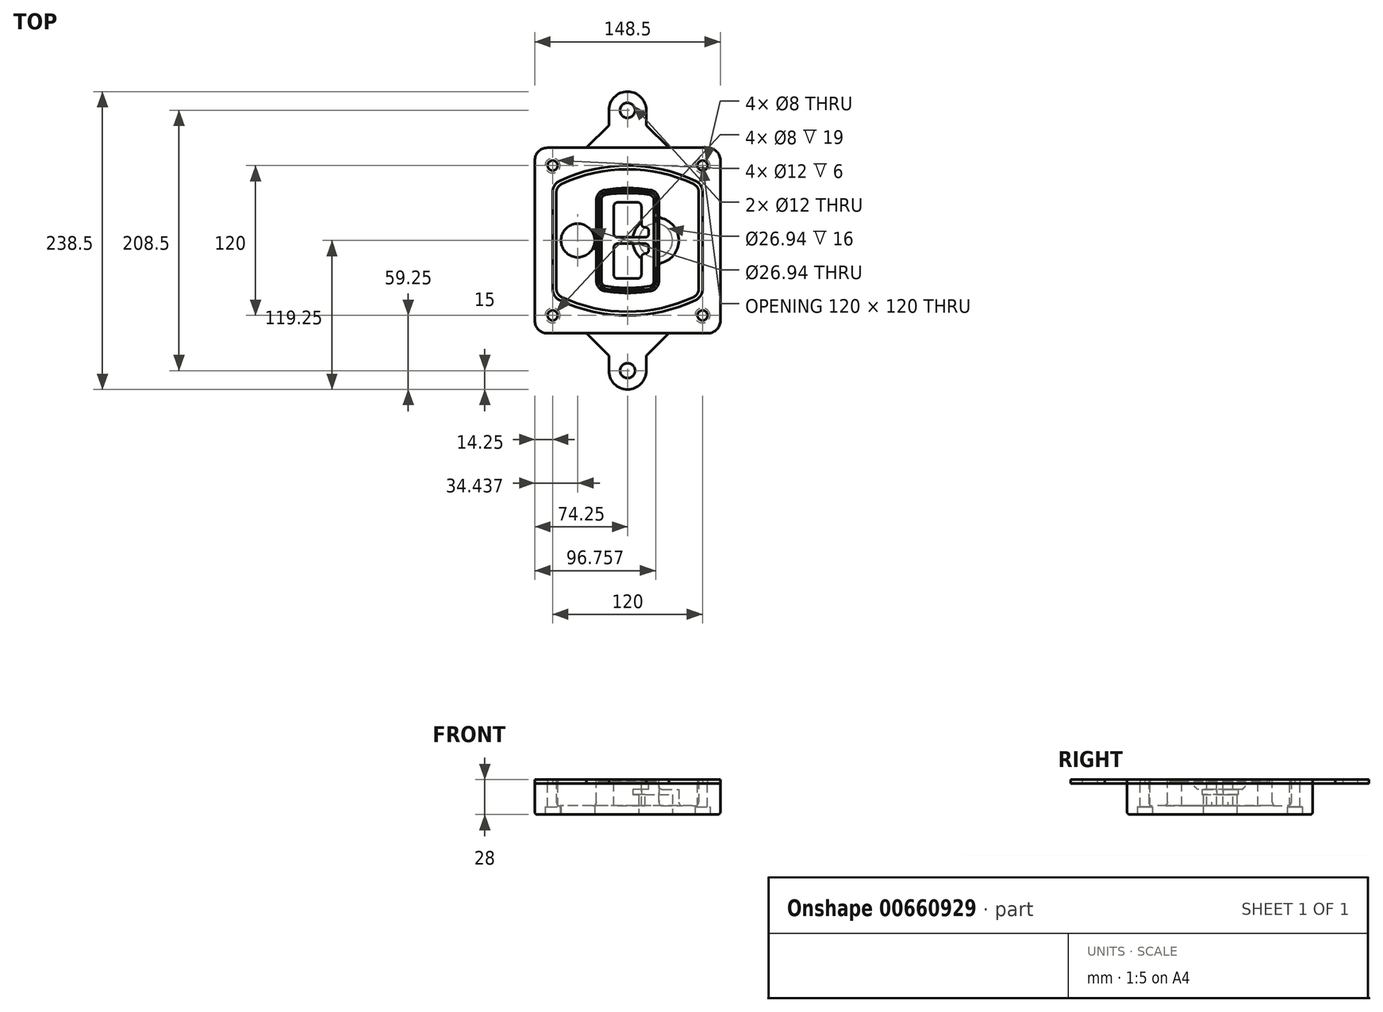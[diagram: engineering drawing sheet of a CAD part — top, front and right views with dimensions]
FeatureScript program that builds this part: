
annotation { "Feature Type Name" : "Feature", "Feature Type Description" : "" }
export const myFeature = defineFeature(function(context is Context, id is Id, definition is map)
    precondition{}
    {
        {
            var Q0;
            Q0=qCreatedBy(makeId("Top.planeOp"),FACE);
            var sketch = newSketch(context, id + "F0", { "sketchPlane" : qUnion([Q0])});
            skPoint(sketch, "E0.rect.middle", {"position": v(0, 0) * mm});
            skLineSegment(sketch, "E1.bottom", {"start": v(-64.25, -74.25) * mm, "end": v(64.25, -74.25) * mm});
            skLineSegment(sketch, "E1.top", {"start": v(-64.25, 74.25) * mm, "end": v(64.25, 74.25) * mm});
            skLineSegment(sketch, "E1.left", {"start": v(-74.25, -64.25) * mm, "end": v(-74.25, 64.25) * mm});
            skLineSegment(sketch, "E1.right", {"start": v(74.25, -64.25) * mm, "end": v(74.25, 64.25) * mm});
            skLineSegment(sketch, "E2", {"start": v(-74.25, 74.25) * mm, "end": v(74.25, -74.25) * mm, "construction": true});
            skLineSegment(sketch, "E3", {"start": v(74.25, 74.25) * mm, "end": v(-74.25, -74.25) * mm, "construction": true});
            skCircle(sketch, "E4", {"center": v(-60, 60) * mm, "radius": 4 * mm});
            skCircle(sketch, "E5", {"center": v(60, 60) * mm, "radius": 4 * mm});
            skCircle(sketch, "E6", {"center": v(60, -60) * mm, "radius": 4 * mm});
            skCircle(sketch, "E7", {"center": v(-60, -60) * mm, "radius": 4 * mm});
            skLineSegment(sketch, "E8", {"start": v(-60, 60) * mm, "end": v(60, 60) * mm, "construction": true});
            skLineSegment(sketch, "E9", {"start": v(60, 60) * mm, "end": v(60, -60) * mm, "construction": true});
            skLineSegment(sketch, "E10", {"start": v(60, -60) * mm, "end": v(-60, -60) * mm, "construction": true});
            skLineSegment(sketch, "E11", {"start": v(-60, -60) * mm, "end": v(-60, 60) * mm, "construction": true});
            skLineSegment(sketch, "E12", {"start": v(-60, 38.83) * mm, "end": v(-60, -38.83) * mm});
            skLineSegment(sketch, "E13", {"start": v(60, 38.83) * mm, "end": v(60, -38.83) * mm});
            skArc(sketch, "E14", {"start": v(54.26, 47.88) * mm, "mid": v(0, 60) * mm, "end": v(-54.26, 47.88) * mm});
            skArc(sketch, "E15", {"start": v(-54.26, -47.88) * mm, "mid": v(0, -60) * mm, "end": v(54.26, -47.88) * mm});
            skLineSegment(sketch, "E16", {"start": v(-60, 0) * mm, "end": v(60, 0) * mm, "construction": true});
            skPoint(sketch, "E17.visualSharp", {"position": v(-60, -45) * mm});
            skArc(sketch, "E17.filletArc", {"start": v(-60, -38.83) * mm, "mid": v(-58.44, -44.2) * mm, "end": v(-54.26, -47.88) * mm});
            skPoint(sketch, "E18.visualSharp", {"position": v(-60, 45) * mm});
            skArc(sketch, "E18.filletArc", {"start": v(-54.26, 47.88) * mm, "mid": v(-58.44, 44.2) * mm, "end": v(-60, 38.83) * mm});
            skPoint(sketch, "E19.visualSharp", {"position": v(60, 45) * mm});
            skArc(sketch, "E19.filletArc", {"start": v(60, 38.83) * mm, "mid": v(58.44, 44.2) * mm, "end": v(54.26, 47.88) * mm});
            skPoint(sketch, "E20.visualSharp", {"position": v(60, -45) * mm});
            skArc(sketch, "E20.filletArc", {"start": v(54.26, -47.88) * mm, "mid": v(58.44, -44.2) * mm, "end": v(60, -38.83) * mm});
            skPoint(sketch, "E21.visualSharp", {"position": v(-74.25, 74.25) * mm});
            skArc(sketch, "E21.filletArc", {"start": v(-64.25, 74.25) * mm, "mid": v(-71.32, 71.32) * mm, "end": v(-74.25, 64.25) * mm});
            skPoint(sketch, "E22.visualSharp", {"position": v(74.25, 74.25) * mm});
            skArc(sketch, "E22.filletArc", {"start": v(74.25, 64.25) * mm, "mid": v(71.32, 71.32) * mm, "end": v(64.25, 74.25) * mm});
            skPoint(sketch, "E23.visualSharp", {"position": v(74.25, -74.25) * mm});
            skArc(sketch, "E23.filletArc", {"start": v(64.25, -74.25) * mm, "mid": v(71.32, -71.32) * mm, "end": v(74.25, -64.25) * mm});
            skPoint(sketch, "E24.visualSharp", {"position": v(-74.25, -74.25) * mm});
            skArc(sketch, "E24.filletArc", {"start": v(-74.25, -64.25) * mm, "mid": v(-71.32, -71.32) * mm, "end": v(-64.25, -74.25) * mm});
            skArc(sketch, "E25.0", {"start": v(57, 38.83) * mm, "mid": v(55.9, 42.58) * mm, "end": v(52.98, 45.17) * mm});
            skLineSegment(sketch, "E25.1", {"start": v(57, 38.83) * mm, "end": v(57, -38.83) * mm});
            skArc(sketch, "E25.2", {"start": v(52.98, -45.17) * mm, "mid": v(55.9, -42.58) * mm, "end": v(57, -38.83) * mm});
            skArc(sketch, "E25.3", {"start": v(-52.98, -45.17) * mm, "mid": v(0, -57) * mm, "end": v(52.98, -45.17) * mm});
            skArc(sketch, "E25.4", {"start": v(-57, -38.83) * mm, "mid": v(-55.9, -42.58) * mm, "end": v(-52.98, -45.17) * mm});
            skArc(sketch, "E25.5", {"start": v(52.98, 45.17) * mm, "mid": v(0, 57) * mm, "end": v(-52.98, 45.17) * mm});
            skLineSegment(sketch, "E25.6", {"start": v(-57, 38.83) * mm, "end": v(-57, -38.83) * mm});
            skArc(sketch, "E25.7", {"start": v(-52.98, 45.17) * mm, "mid": v(-55.9, 42.58) * mm, "end": v(-57, 38.83) * mm});
            skArc(sketch, "E26.0", {"start": v(-55.96, 51.5) * mm, "mid": v(-61.82, 46.33) * mm, "end": v(-64, 38.83) * mm});
            skArc(sketch, "E26.1", {"start": v(55.96, 51.5) * mm, "mid": v(0, 64) * mm, "end": v(-55.96, 51.5) * mm});
            skArc(sketch, "E26.2", {"start": v(64, 38.83) * mm, "mid": v(61.82, 46.33) * mm, "end": v(55.96, 51.5) * mm});
            skLineSegment(sketch, "E26.3", {"start": v(64, 38.83) * mm, "end": v(64, -38.83) * mm});
            skArc(sketch, "E26.4", {"start": v(55.96, -51.5) * mm, "mid": v(61.82, -46.33) * mm, "end": v(64, -38.83) * mm});
            skLineSegment(sketch, "E26.5", {"start": v(-64, 38.83) * mm, "end": v(-64, -38.83) * mm});
            skArc(sketch, "E26.6", {"start": v(-55.96, -51.5) * mm, "mid": v(0, -64) * mm, "end": v(55.96, -51.5) * mm});
            skArc(sketch, "E26.7", {"start": v(-64, -38.83) * mm, "mid": v(-61.82, -46.33) * mm, "end": v(-55.96, -51.5) * mm});
            skSolve(sketch);
        }
        {
            var Q0;
            Q0=makeQuery(id+"F0.imprint","IMPRINT",FACE,{"disambiguationData":[TD([[makeQuery(id+"F0.imprint","IMPRINT",EDGE,{"derivedFrom":sQuery(id+"F0.wireOp",EDGE,"E1.bottom")}),1.0]])]});
            var Q1;
            Q1=makeQuery(id+"F0.imprint","IMPRINT",FACE,{"disambiguationData":[TD([[makeQuery(id+"F0.imprint","IMPRINT",EDGE,{"derivedFrom":sQuery(id+"F0.wireOp",EDGE,"E12")}),1.0]])]});
            var Q2;
            Q2=makeQuery(id+"F0.imprint","IMPRINT",FACE,{"disambiguationData":[TD([[makeQuery(id+"F0.imprint","IMPRINT",EDGE,{"derivedFrom":sQuery(id+"F0.wireOp",EDGE,"E25.0")}),1.0]])]});
            var Q3;
            Q3=makeQuery(id+"F0.imprint","IMPRINT",FACE,{"disambiguationData":[TD([[makeQuery(id+"F0.imprint","IMPRINT",EDGE,{"derivedFrom":sQuery(id+"F0.wireOp",EDGE,"E12")}),-1.0]])]});
            extrude(context, id + "F1", {"entities" : qUnion([Q0, Q1, Q2, Q3]), "oppositeDirection" : true, "depth" : 25 * mm, "offsetDistance" : 25 * mm});
        }
        {
            var Q0;
            Q0=makeQuery(id+"F0.imprint","IMPRINT",FACE,{"disambiguationData":[TD([[makeQuery(id+"F0.imprint","IMPRINT",EDGE,{"derivedFrom":sQuery(id+"F0.wireOp",EDGE,"E12")}),1.0]])]});
            extrude(context, id + "F2", {"entities" : qUnion([Q0]), "operationType" : NewBodyOperationType.ADD, "depth" : 3 * mm});
        }
        {
            var Q0;
            Q0=makeQuery(id+"F0.imprint","IMPRINT",FACE,{"disambiguationData":[TD([[makeQuery(id+"F0.imprint","IMPRINT",EDGE,{"derivedFrom":sQuery(id+"F0.wireOp",EDGE,"E25.0")}),1.0]])]});
            extrude(context, id + "F3", {"entities" : qUnion([Q0]), "operationType" : NewBodyOperationType.REMOVE, "oppositeDirection" : true, "depth" : 18 * mm});
        }
        {
            var Q0;
            Q0=makeQuery(id+"F2.opExtrude","CAP_FACE",FACE,{"disambiguationData":[OSD([sQuery(id+"F0.wireOp",EDGE,"E12"),sQuery(id+"F0.wireOp",EDGE,"E13"),sQuery(id+"F0.wireOp",EDGE,"E14"),sQuery(id+"F0.wireOp",EDGE,"E15"),sQuery(id+"F0.wireOp",EDGE,"E17.filletArc"),sQuery(id+"F0.wireOp",EDGE,"E18.filletArc"),sQuery(id+"F0.wireOp",EDGE,"E19.filletArc"),sQuery(id+"F0.wireOp",EDGE,"E20.filletArc"),sQuery(id+"F0.wireOp",EDGE,"E25.0"),sQuery(id+"F0.wireOp",EDGE,"E25.1"),sQuery(id+"F0.wireOp",EDGE,"E25.2"),sQuery(id+"F0.wireOp",EDGE,"E25.3"),sQuery(id+"F0.wireOp",EDGE,"E25.4"),sQuery(id+"F0.wireOp",EDGE,"E25.5"),sQuery(id+"F0.wireOp",EDGE,"E25.6"),sQuery(id+"F0.wireOp",EDGE,"E25.7")])],"isStart":false});
            var sketch = newSketch(context, id + "F4", { "sketchPlane" : qUnion([Q0])});
            skArc(sketch, "E27.0", {"start": v(-18.34, -40.45) * mm, "mid": v(0, -42) * mm, "end": v(18.34, -40.45) * mm});
            skArc(sketch, "E28.0", {"start": v(18.34, 40.45) * mm, "mid": v(0, 42) * mm, "end": v(-18.34, 40.45) * mm});
            skLineSegment(sketch, "E29", {"start": v(-25, 32.57) * mm, "end": v(-25, -32.57) * mm});
            skLineSegment(sketch, "E30", {"start": v(25, 32.57) * mm, "end": v(25, -32.57) * mm});
            skLineSegment(sketch, "E31", {"start": v(-25, 39.1) * mm, "end": v(25, 39.1) * mm, "construction": true});
            skLineSegment(sketch, "E32", {"start": v(-25, -39.1) * mm, "end": v(25, -39.1) * mm, "construction": true});
            skPoint(sketch, "E33.visualSharp", {"position": v(-25, 39.1) * mm});
            skArc(sketch, "E33.filletArc", {"start": v(-18.34, 40.45) * mm, "mid": v(-23.11, 37.73) * mm, "end": v(-25, 32.57) * mm});
            skPoint(sketch, "E34.visualSharp", {"position": v(25, 39.1) * mm});
            skArc(sketch, "E34.filletArc", {"start": v(25, 32.57) * mm, "mid": v(23.11, 37.73) * mm, "end": v(18.34, 40.45) * mm});
            skPoint(sketch, "E35.visualSharp", {"position": v(25, -39.1) * mm});
            skArc(sketch, "E35.filletArc", {"start": v(18.34, -40.45) * mm, "mid": v(23.11, -37.73) * mm, "end": v(25, -32.57) * mm});
            skPoint(sketch, "E36.visualSharp", {"position": v(-25, -39.1) * mm});
            skArc(sketch, "E36.filletArc", {"start": v(-25, -32.57) * mm, "mid": v(-23.11, -37.73) * mm, "end": v(-18.34, -40.45) * mm});
            skArc(sketch, "E37.0", {"start": v(52.98, 45.17) * mm, "mid": v(0, 57) * mm, "end": v(-52.98, 45.17) * mm});
            skArc(sketch, "E37.1", {"start": v(-52.98, 45.17) * mm, "mid": v(-55.9, 42.58) * mm, "end": v(-57, 38.83) * mm});
            skLineSegment(sketch, "E37.2", {"start": v(-57, 38.83) * mm, "end": v(-57, -38.83) * mm});
            skArc(sketch, "E37.3", {"start": v(-57, -38.83) * mm, "mid": v(-55.9, -42.58) * mm, "end": v(-52.98, -45.17) * mm});
            skArc(sketch, "E37.4", {"start": v(-52.98, -45.17) * mm, "mid": v(0, -57) * mm, "end": v(52.98, -45.17) * mm});
            skArc(sketch, "E37.5", {"start": v(52.98, -45.17) * mm, "mid": v(55.9, -42.58) * mm, "end": v(57, -38.83) * mm});
            skLineSegment(sketch, "E37.6", {"start": v(57, 38.83) * mm, "end": v(57, -38.83) * mm});
            skArc(sketch, "E37.7", {"start": v(57, 38.83) * mm, "mid": v(55.9, 42.58) * mm, "end": v(52.98, 45.17) * mm});
            skLineSegment(sketch, "E38.0", {"start": v(23, 32.57) * mm, "end": v(23, -32.57) * mm});
            skArc(sketch, "E38.1", {"start": v(18, -38.48) * mm, "mid": v(21.58, -36.44) * mm, "end": v(23, -32.57) * mm});
            skArc(sketch, "E38.2", {"start": v(-18, -38.48) * mm, "mid": v(0, -40) * mm, "end": v(18, -38.48) * mm});
            skArc(sketch, "E38.3", {"start": v(-23, -32.57) * mm, "mid": v(-21.58, -36.44) * mm, "end": v(-18, -38.48) * mm});
            skLineSegment(sketch, "E38.4", {"start": v(-23, 32.57) * mm, "end": v(-23, -32.57) * mm});
            skArc(sketch, "E38.5", {"start": v(23, 32.57) * mm, "mid": v(21.58, 36.44) * mm, "end": v(18, 38.48) * mm});
            skArc(sketch, "E38.6", {"start": v(-18, 38.48) * mm, "mid": v(-21.58, 36.44) * mm, "end": v(-23, 32.57) * mm});
            skArc(sketch, "E38.7", {"start": v(18, 38.48) * mm, "mid": v(0, 40) * mm, "end": v(-18, 38.48) * mm});
            skArc(sketch, "E39.0", {"start": v(21, 32.57) * mm, "mid": v(20.06, 35.15) * mm, "end": v(17.67, 36.5) * mm});
            skLineSegment(sketch, "E39.1", {"start": v(21, 32.57) * mm, "end": v(21, -32.57) * mm});
            skArc(sketch, "E39.2", {"start": v(17.67, -36.5) * mm, "mid": v(20.06, -35.15) * mm, "end": v(21, -32.57) * mm});
            skArc(sketch, "E39.3", {"start": v(-17.67, -36.5) * mm, "mid": v(0, -38) * mm, "end": v(17.67, -36.5) * mm});
            skArc(sketch, "E39.4", {"start": v(-21, -32.57) * mm, "mid": v(-20.06, -35.15) * mm, "end": v(-17.67, -36.5) * mm});
            skArc(sketch, "E39.5", {"start": v(17.67, 36.5) * mm, "mid": v(0, 38) * mm, "end": v(-17.67, 36.5) * mm});
            skLineSegment(sketch, "E39.6", {"start": v(-21, 32.57) * mm, "end": v(-21, -32.57) * mm});
            skArc(sketch, "E39.7", {"start": v(-17.67, 36.5) * mm, "mid": v(-20.06, 35.15) * mm, "end": v(-21, 32.57) * mm});
            skLineSegment(sketch, "E40", {"start": v(-25, 0) * mm, "end": v(25, 0) * mm, "construction": true});
            skLineSegment(sketch, "E41", {"start": v(-11, 5.5) * mm, "end": v(-11, 27.5) * mm});
            skLineSegment(sketch, "E42", {"start": v(-8, 30.5) * mm, "end": v(8, 30.5) * mm});
            skLineSegment(sketch, "E43", {"start": v(11, 27.5) * mm, "end": v(11, 13.5) * mm});
            skLineSegment(sketch, "E44", {"start": v(14, 10.5) * mm, "end": v(14, 10.5) * mm});
            skLineSegment(sketch, "E45", {"start": v(17, 7.5) * mm, "end": v(17, 5.5) * mm});
            skLineSegment(sketch, "E46", {"start": v(14, 2.5) * mm, "end": v(-8, 2.5) * mm});
            skPoint(sketch, "E47.visualSharp", {"position": v(-11, 30.5) * mm});
            skArc(sketch, "E47.filletArc", {"start": v(-8, 30.5) * mm, "mid": v(-10.12, 29.62) * mm, "end": v(-11, 27.5) * mm});
            skPoint(sketch, "E48.visualSharp", {"position": v(11, 30.5) * mm});
            skArc(sketch, "E48.filletArc", {"start": v(11, 27.5) * mm, "mid": v(10.12, 29.62) * mm, "end": v(8, 30.5) * mm});
            skPoint(sketch, "E49.visualSharp", {"position": v(11, 10.5) * mm});
            skArc(sketch, "E49.filletArc", {"start": v(11, 13.5) * mm, "mid": v(11.88, 11.38) * mm, "end": v(14, 10.5) * mm});
            skPoint(sketch, "E50.visualSharp", {"position": v(17, 10.5) * mm});
            skArc(sketch, "E50.filletArc", {"start": v(17, 7.5) * mm, "mid": v(16.12, 9.62) * mm, "end": v(14, 10.5) * mm});
            skPoint(sketch, "E51.visualSharp", {"position": v(17, 2.5) * mm});
            skArc(sketch, "E51.filletArc", {"start": v(14, 2.5) * mm, "mid": v(16.12, 3.38) * mm, "end": v(17, 5.5) * mm});
            skPoint(sketch, "E52.visualSharp", {"position": v(-11, 2.5) * mm});
            skArc(sketch, "E52.filletArc", {"start": v(-11, 5.5) * mm, "mid": v(-10.12, 3.38) * mm, "end": v(-8, 2.5) * mm});
            skLineSegment(sketch, "E53.0.MirrorCS", {"start": v(14, -2.5) * mm, "end": v(-8, -2.5) * mm});
            skArc(sketch, "E54.0.MirrorCS", {"start": v(-11, -5.5) * mm, "mid": v(-10.12, -3.38) * mm, "end": v(-8, -2.5) * mm});
            skLineSegment(sketch, "E55.0.MirrorCS", {"start": v(-11, -5.5) * mm, "end": v(-11, -27.5) * mm});
            skArc(sketch, "E56.0.MirrorCS", {"start": v(-8, -30.5) * mm, "mid": v(-10.12, -29.62) * mm, "end": v(-11, -27.5) * mm});
            skLineSegment(sketch, "E57.0.MirrorCS", {"start": v(-8, -30.5) * mm, "end": v(8, -30.5) * mm});
            skArc(sketch, "E58.0.MirrorCS", {"start": v(11, -27.5) * mm, "mid": v(10.12, -29.62) * mm, "end": v(8, -30.5) * mm});
            skLineSegment(sketch, "E59.0.MirrorCS", {"start": v(11, -27.5) * mm, "end": v(11, -13.5) * mm});
            skArc(sketch, "E60.0.MirrorCS", {"start": v(11, -13.5) * mm, "mid": v(11.88, -11.38) * mm, "end": v(14, -10.5) * mm});
            skArc(sketch, "E61.0.MirrorCS", {"start": v(17, -7.5) * mm, "mid": v(16.12, -9.62) * mm, "end": v(14, -10.5) * mm});
            skLineSegment(sketch, "E62.0.MirrorCS", {"start": v(17, -7.5) * mm, "end": v(17, -5.5) * mm});
            skArc(sketch, "E63.0.MirrorCS", {"start": v(14, -2.5) * mm, "mid": v(16.12, -3.38) * mm, "end": v(17, -5.5) * mm});
            skSolve(sketch);
        }
        {
            var Q0;
            Q0=makeQuery(id+"F4.imprint","IMPRINT",FACE,{"disambiguationData":[TD([[makeQuery(id+"F4.imprint","IMPRINT",EDGE,{"derivedFrom":sQuery(id+"F4.wireOp",EDGE,"E27.0")}),1.0]])]});
            var Q1;
            Q1=makeQuery(id+"F4.imprint","IMPRINT",FACE,{"disambiguationData":[TD([[makeQuery(id+"F4.imprint","IMPRINT",EDGE,{"derivedFrom":sQuery(id+"F4.wireOp",EDGE,"E38.0")}),-1.0]])]});
            var Q2;
            Q2=makeQuery(id+"F4.imprint","IMPRINT",FACE,{"disambiguationData":[TD([[makeQuery(id+"F4.imprint","IMPRINT",EDGE,{"derivedFrom":sQuery(id+"F4.wireOp",EDGE,"E39.0")}),1.0]])]});
            extrude(context, id + "F5", {"entities" : qUnion([Q0, Q1, Q2]), "operationType" : NewBodyOperationType.ADD, "endBound" : BoundingType.UP_TO_NEXT, "oppositeDirection" : true, "depth" : 25 * mm});
        }
        {
            var Q0;
            Q0=makeQuery(id+"F4.imprint","IMPRINT",FACE,{"disambiguationData":[TD([[makeQuery(id+"F4.imprint","IMPRINT",EDGE,{"derivedFrom":sQuery(id+"F4.wireOp",EDGE,"E38.0")}),-1.0]])]});
            extrude(context, id + "F6", {"entities" : qUnion([Q0]), "operationType" : NewBodyOperationType.REMOVE, "oppositeDirection" : true, "depth" : 2 * mm});
        }
        {
            var Q0;
            Q0=makeQuery(id+"F1.opExtrude","CAP_FACE",FACE,{"disambiguationData":[OSD([sQuery(id+"F0.wireOp",EDGE,"E1.bottom"),sQuery(id+"F0.wireOp",EDGE,"E1.top"),sQuery(id+"F0.wireOp",EDGE,"E1.left"),sQuery(id+"F0.wireOp",EDGE,"E1.right"),sQuery(id+"F0.wireOp",EDGE,"E4"),sQuery(id+"F0.wireOp",EDGE,"E5"),sQuery(id+"F0.wireOp",EDGE,"E6"),sQuery(id+"F0.wireOp",EDGE,"E7"),sQuery(id+"F0.wireOp",EDGE,"E21.filletArc"),sQuery(id+"F0.wireOp",EDGE,"E22.filletArc"),sQuery(id+"F0.wireOp",EDGE,"E23.filletArc"),sQuery(id+"F0.wireOp",EDGE,"E24.filletArc")])],"isStart":false});
            var sketch = newSketch(context, id + "F7", { "sketchPlane" : qUnion([Q0])});
            skCircle(sketch, "E64", {"center": v(22.5, 0) * mm, "radius": 13.47 * mm});
            skCircle(sketch, "E65", {"center": v(-39.81, 0) * mm, "radius": 13.47 * mm});
            skLineSegment(sketch, "E66", {"start": v(74.25, 0) * mm, "end": v(-74.25, 0) * mm});
            skCircle(sketch, "E67", {"center": v(22.5, 0) * mm, "radius": 18.47 * mm});
            skCircle(sketch, "E68", {"center": v(60, -60) * mm, "radius": 6 * mm});
            skCircle(sketch, "E69", {"center": v(-60, -60) * mm, "radius": 6 * mm});
            skCircle(sketch, "E70", {"center": v(-60, 60) * mm, "radius": 6 * mm});
            skCircle(sketch, "E71", {"center": v(60, 60) * mm, "radius": 6 * mm});
            skSolve(sketch);
        }
        {
            var Q0;
            {var subQ1=sQuery(id+"F7.wireOp",EDGE,"E66");var subQ4=sQuery(id+"F7.wireOp",EDGE,"E64");var subQ6=makeQuery(id+"F7.imprint","INTERSECT",VERTEX,{"disambiguationData":[OD(0.0)],"derivedFrom":[subQ4,subQ1]});Q0=makeQuery(id+"F7.imprint","IMPRINT",FACE,{"disambiguationData":[TD([[makeQuery(id+"F7.imprint","IMPRINT",EDGE,{"disambiguationData":[TD([[subQ6,-1.0]])],"derivedFrom":subQ4}),-1.0]])]});}
            var Q1;
            {var subQ0=sQuery(id+"F7.wireOp",EDGE,"E66");var subQ1=sQuery(id+"F7.wireOp",EDGE,"E64");var subQ3=makeQuery(id+"F7.imprint","INTERSECT",VERTEX,{"disambiguationData":[OD(0.0)],"derivedFrom":[subQ1,subQ0]});Q1=makeQuery(id+"F7.imprint","IMPRINT",FACE,{"disambiguationData":[TD([[makeQuery(id+"F7.imprint","IMPRINT",EDGE,{"disambiguationData":[TD([[subQ3,-1.0]])],"derivedFrom":subQ1}),1.0]])]});}
            var Q2;
            {var subQ0=sQuery(id+"F7.wireOp",EDGE,"E66");var subQ1=sQuery(id+"F7.wireOp",EDGE,"E64");var subQ3=makeQuery(id+"F7.imprint","INTERSECT",VERTEX,{"disambiguationData":[OD(0.0)],"derivedFrom":[subQ1,subQ0]});Q2=makeQuery(id+"F7.imprint","IMPRINT",FACE,{"disambiguationData":[TD([[makeQuery(id+"F7.imprint","IMPRINT",EDGE,{"disambiguationData":[TD([[subQ3,1.0]])],"derivedFrom":subQ1}),1.0]])]});}
            var Q3;
            {var subQ1=sQuery(id+"F7.wireOp",EDGE,"E66");var subQ4=sQuery(id+"F7.wireOp",EDGE,"E64");var subQ6=makeQuery(id+"F7.imprint","INTERSECT",VERTEX,{"disambiguationData":[OD(0.0)],"derivedFrom":[subQ4,subQ1]});Q3=makeQuery(id+"F7.imprint","IMPRINT",FACE,{"disambiguationData":[TD([[makeQuery(id+"F7.imprint","IMPRINT",EDGE,{"disambiguationData":[TD([[subQ6,1.0]])],"derivedFrom":subQ4}),-1.0]])]});}
            extrude(context, id + "F8", {"entities" : qUnion([Q0, Q1, Q2, Q3]), "operationType" : NewBodyOperationType.ADD, "oppositeDirection" : true, "depth" : 20 * mm});
        }
        {
            var Q0;
            {var subQ0=sQuery(id+"F7.wireOp",EDGE,"E66");var subQ1=sQuery(id+"F7.wireOp",EDGE,"E64");var subQ3=makeQuery(id+"F7.imprint","INTERSECT",VERTEX,{"disambiguationData":[OD(0.0)],"derivedFrom":[subQ1,subQ0]});Q0=makeQuery(id+"F7.imprint","IMPRINT",FACE,{"disambiguationData":[TD([[makeQuery(id+"F7.imprint","IMPRINT",EDGE,{"disambiguationData":[TD([[subQ3,-1.0]])],"derivedFrom":subQ1}),1.0]])]});}
            var Q1;
            {var subQ0=sQuery(id+"F7.wireOp",EDGE,"E66");var subQ1=sQuery(id+"F7.wireOp",EDGE,"E64");var subQ3=makeQuery(id+"F7.imprint","INTERSECT",VERTEX,{"disambiguationData":[OD(0.0)],"derivedFrom":[subQ1,subQ0]});Q1=makeQuery(id+"F7.imprint","IMPRINT",FACE,{"disambiguationData":[TD([[makeQuery(id+"F7.imprint","IMPRINT",EDGE,{"disambiguationData":[TD([[subQ3,1.0]])],"derivedFrom":subQ1}),1.0]])]});}
            extrude(context, id + "F9", {"entities" : qUnion([Q0, Q1]), "operationType" : NewBodyOperationType.REMOVE, "oppositeDirection" : true, "depth" : 16 * mm});
        }
        {
            var Q0;
            {var subQ0=sQuery(id+"F7.wireOp",EDGE,"E66");var subQ1=sQuery(id+"F7.wireOp",EDGE,"E65");var subQ3=makeQuery(id+"F7.imprint","INTERSECT",VERTEX,{"disambiguationData":[OD(0.0)],"derivedFrom":[subQ1,subQ0]});Q0=makeQuery(id+"F7.imprint","IMPRINT",FACE,{"disambiguationData":[TD([[makeQuery(id+"F7.imprint","IMPRINT",EDGE,{"disambiguationData":[TD([[subQ3,-1.0]])],"derivedFrom":subQ1}),1.0]])]});}
            var Q1;
            {var subQ0=sQuery(id+"F7.wireOp",EDGE,"E66");var subQ1=sQuery(id+"F7.wireOp",EDGE,"E65");var subQ3=makeQuery(id+"F7.imprint","INTERSECT",VERTEX,{"disambiguationData":[OD(0.0)],"derivedFrom":[subQ1,subQ0]});Q1=makeQuery(id+"F7.imprint","IMPRINT",FACE,{"disambiguationData":[TD([[makeQuery(id+"F7.imprint","IMPRINT",EDGE,{"disambiguationData":[TD([[subQ3,1.0]])],"derivedFrom":subQ1}),1.0]])]});}
            extrude(context, id + "F10", {"entities" : qUnion([Q0, Q1]), "operationType" : NewBodyOperationType.REMOVE, "oppositeDirection" : true, "depth" : 25 * mm});
        }
        {
            var Q0;
            Q0=makeQuery(id+"F7.imprint","IMPRINT",FACE,{"disambiguationData":[TD([[makeQuery(id+"F7.imprint","IMPRINT",EDGE,{"derivedFrom":sQuery(id+"F7.wireOp",EDGE,"E68")}),1.0]])]});
            var Q1;
            Q1=makeQuery(id+"F7.imprint","IMPRINT",FACE,{"disambiguationData":[TD([[makeQuery(id+"F7.imprint","IMPRINT",EDGE,{"derivedFrom":makeQuery(id+"F1.opExtrude","CAP_EDGE",EDGE,{"disambiguationData":[OSD([sQuery(id+"F0.wireOp",EDGE,"E5")])],"isStart":false})}),-1.0]])]});
            var Q2;
            Q2=makeQuery(id+"F7.imprint","IMPRINT",FACE,{"disambiguationData":[TD([[makeQuery(id+"F7.imprint","IMPRINT",EDGE,{"derivedFrom":sQuery(id+"F7.wireOp",EDGE,"E69")}),1.0]])]});
            var Q3;
            Q3=makeQuery(id+"F7.imprint","IMPRINT",FACE,{"disambiguationData":[TD([[makeQuery(id+"F7.imprint","IMPRINT",EDGE,{"derivedFrom":makeQuery(id+"F1.opExtrude","CAP_EDGE",EDGE,{"disambiguationData":[OSD([sQuery(id+"F0.wireOp",EDGE,"E4")])],"isStart":false})}),-1.0]])]});
            var Q4;
            Q4=makeQuery(id+"F7.imprint","IMPRINT",FACE,{"disambiguationData":[TD([[makeQuery(id+"F7.imprint","IMPRINT",EDGE,{"derivedFrom":sQuery(id+"F7.wireOp",EDGE,"E70")}),1.0]])]});
            var Q5;
            Q5=makeQuery(id+"F7.imprint","IMPRINT",FACE,{"disambiguationData":[TD([[makeQuery(id+"F7.imprint","IMPRINT",EDGE,{"derivedFrom":makeQuery(id+"F1.opExtrude","CAP_EDGE",EDGE,{"disambiguationData":[OSD([sQuery(id+"F0.wireOp",EDGE,"E7")])],"isStart":false})}),-1.0]])]});
            var Q6;
            Q6=makeQuery(id+"F7.imprint","IMPRINT",FACE,{"disambiguationData":[TD([[makeQuery(id+"F7.imprint","IMPRINT",EDGE,{"derivedFrom":sQuery(id+"F7.wireOp",EDGE,"E71")}),1.0]])]});
            var Q7;
            Q7=makeQuery(id+"F7.imprint","IMPRINT",FACE,{"disambiguationData":[TD([[makeQuery(id+"F7.imprint","IMPRINT",EDGE,{"derivedFrom":makeQuery(id+"F1.opExtrude","CAP_EDGE",EDGE,{"disambiguationData":[OSD([sQuery(id+"F0.wireOp",EDGE,"E6")])],"isStart":false})}),-1.0]])]});
            extrude(context, id + "F11", {"entities" : qUnion([Q0, Q1, Q2, Q3, Q4, Q5, Q6, Q7]), "operationType" : NewBodyOperationType.REMOVE, "oppositeDirection" : true, "depth" : 6 * mm});
        }
        {
            var Q0;
            Q0=makeQuery(id+"F9.boolean.opBoolean","COPY",FACE,{"derivedFrom":makeQuery(id+"F9.opExtrude","CAP_FACE",FACE,{"disambiguationData":[OSD([sQuery(id+"F7.wireOp",EDGE,"E64")])],"isStart":false})});
            var sketch = newSketch(context, id + "F12", { "sketchPlane" : qUnion([Q0])});
            skArc(sketch, "E72.0", {"start": v(11, 14.45) * mm, "mid": v(6.45, 9.13) * mm, "end": v(4.2, 2.5) * mm});
            skArc(sketch, "E72.1", {"start": v(4.2, -2.5) * mm, "mid": v(6.45, -9.13) * mm, "end": v(11, -14.45) * mm});
            skLineSegment(sketch, "E73", {"start": v(4.2, -2.5) * mm, "end": v(14, -2.5) * mm});
            skLineSegment(sketch, "E74.0", {"start": v(14, 2.5) * mm, "end": v(4.2, 2.5) * mm});
            skArc(sketch, "E74.1", {"start": v(14, 2.5) * mm, "mid": v(16.12, 3.38) * mm, "end": v(17, 5.5) * mm});
            skLineSegment(sketch, "E74.2", {"start": v(17, 7.5) * mm, "end": v(17, 5.5) * mm});
            skArc(sketch, "E74.3", {"start": v(17, 7.5) * mm, "mid": v(16.12, 9.62) * mm, "end": v(14, 10.5) * mm});
            skArc(sketch, "E74.4", {"start": v(11, 13.5) * mm, "mid": v(11.88, 11.38) * mm, "end": v(14, 10.5) * mm});
            skLineSegment(sketch, "E74.5", {"start": v(11, 14.45) * mm, "end": v(11, 13.5) * mm});
            skLineSegment(sketch, "E74.7", {"start": v(14, -2.5) * mm, "end": v(4.2, -2.5) * mm});
            skArc(sketch, "E74.8", {"start": v(14, -2.5) * mm, "mid": v(16.12, -3.38) * mm, "end": v(17, -5.5) * mm});
            skLineSegment(sketch, "E74.9", {"start": v(17, -7.5) * mm, "end": v(17, -5.5) * mm});
            skArc(sketch, "E74.10", {"start": v(17, -7.5) * mm, "mid": v(16.12, -9.62) * mm, "end": v(14, -10.5) * mm});
            skArc(sketch, "E74.11", {"start": v(11, -13.5) * mm, "mid": v(11.88, -11.38) * mm, "end": v(14, -10.5) * mm});
            skLineSegment(sketch, "E74.12", {"start": v(11, -14.45) * mm, "end": v(11, -13.5) * mm});
            skPoint(sketch, "E75.orphan", {"position": v(11, -27.5) * mm});
            skPoint(sketch, "E76.orphan", {"position": v(-8, -2.5) * mm});
            skPoint(sketch, "E77.orphan", {"position": v(-8, 2.5) * mm});
            skPoint(sketch, "E78.orphan", {"position": v(11, 27.5) * mm});
            skSolve(sketch);
        }
        {
            var Q0;
            {var subQ7=sQuery(id+"F12.wireOp",EDGE,"E72.0");var subQ14=sQuery(id+"F12.wireOp",EDGE,"E72.1");var subQ16=sQuery(id+"F12.wireOp",EDGE,"E74.1");var subQ18=sQuery(id+"F12.wireOp",EDGE,"E74.8");Q0=qUnion([makeQuery(id+"F12.imprint","IMPRINT",FACE,{"disambiguationData":[TD([[makeQuery(id+"F12.imprint","IMPRINT",EDGE,{"derivedFrom":subQ7}),1.0]])]}),makeQuery(id+"F12.imprint","IMPRINT",FACE,{"disambiguationData":[TD([[makeQuery(id+"F12.imprint","IMPRINT",EDGE,{"derivedFrom":subQ14}),1.0]])]}),makeQuery(id+"F12.imprint","IMPRINT",FACE,{"disambiguationData":[TD([[makeQuery(id+"F12.imprint","IMPRINT",EDGE,{"derivedFrom":subQ16}),1.0]])]}),makeQuery(id+"F12.imprint","IMPRINT",FACE,{"disambiguationData":[TD([[makeQuery(id+"F12.imprint","IMPRINT",EDGE,{"derivedFrom":subQ18}),-1.0]])]})]);}
            var Q1;
            Q1=makeQuery(id+"F5.boolean.opBoolean","SPLIT",FACE,{"disambiguationData":[TD([makeQuery(id+"F5.opExtrude","SWEPT_FACE",FACE,{"disambiguationData":[OSD([sQuery(id+"F4.wireOp",EDGE,"E41")])]})])],"derivedFrom":makeQuery(id+"F3.boolean.opBoolean","COPY",FACE,{"derivedFrom":makeQuery(id+"F3.opExtrude","CAP_FACE",FACE,{"disambiguationData":[OSD([sQuery(id+"F0.wireOp",EDGE,"E25.0"),sQuery(id+"F0.wireOp",EDGE,"E25.1"),sQuery(id+"F0.wireOp",EDGE,"E25.2"),sQuery(id+"F0.wireOp",EDGE,"E25.3"),sQuery(id+"F0.wireOp",EDGE,"E25.4"),sQuery(id+"F0.wireOp",EDGE,"E25.5"),sQuery(id+"F0.wireOp",EDGE,"E25.6"),sQuery(id+"F0.wireOp",EDGE,"E25.7")])],"isStart":false})})});
            extrude(context, id + "F13", {"entities" : qUnion([Q0]), "operationType" : NewBodyOperationType.REMOVE, "endBound" : BoundingType.UP_TO_SURFACE, "endBoundEntityFace" : qUnion([Q1]), "depth" : 25 * mm});
        }
        {
            var Q0;
            Q0=makeQuery(id+"F3.boolean.opBoolean","COPY",EDGE,{"derivedFrom":makeQuery(id+"F3.opExtrude","CAP_EDGE",EDGE,{"disambiguationData":[OSD([sQuery(id+"F0.wireOp",EDGE,"E25.6")])],"isStart":false})});
            var Q1;
            Q1=makeQuery(id+"F8.boolean.opBoolean","INTERSECT",EDGE,{"derivedFrom":[makeQuery(id+"F5.opExtrude","SWEPT_FACE",FACE,{"disambiguationData":[OSD([sQuery(id+"F4.wireOp",EDGE,"E30")])]}),makeQuery(id+"F8.opExtrude","CAP_FACE",FACE,{"disambiguationData":[OSD([sQuery(id+"F7.wireOp",EDGE,"E67")])],"isStart":false})]});
            var Q2;
            Q2=makeQuery(id+"F8.boolean.opBoolean","INTERSECT",EDGE,{"disambiguationData":[OD(1.0)],"derivedFrom":[makeQuery(id+"F5.opExtrude","SWEPT_FACE",FACE,{"disambiguationData":[OSD([sQuery(id+"F4.wireOp",EDGE,"E30")])]}),makeQuery(id+"F8.opExtrude","SWEPT_FACE",FACE,{"disambiguationData":[OSD([sQuery(id+"F7.wireOp",EDGE,"E67")])]})]});
            var Q3;
            {var subQ0=sQuery(id+"F4.wireOp",EDGE,"E30");Q3=makeQuery(id+"F8.boolean.opBoolean","SPLIT",EDGE,{"disambiguationData":[TD([makeQuery(id+"F5.opExtrude","SWEPT_FACE",FACE,{"disambiguationData":[OSD([sQuery(id+"F4.wireOp",EDGE,"E35.filletArc")])]})])],"derivedFrom":makeQuery(id+"F5.opExtrude","CAP_EDGE",EDGE,{"disambiguationData":[OSD([subQ0])],"isStart":false})});}
            var Q4;
            {var subQ0=sQuery(id+"F0.wireOp",EDGE,"E25.7");var subQ1=sQuery(id+"F0.wireOp",EDGE,"E25.1");var subQ2=sQuery(id+"F0.wireOp",EDGE,"E25.6");var subQ3=sQuery(id+"F0.wireOp",EDGE,"E25.5");var subQ4=sQuery(id+"F0.wireOp",EDGE,"E25.4");var subQ5=sQuery(id+"F0.wireOp",EDGE,"E25.0");var subQ6=sQuery(id+"F0.wireOp",EDGE,"E25.2");var subQ7=sQuery(id+"F0.wireOp",EDGE,"E25.3");Q4=makeQuery(id+"F8.boolean.opBoolean","INTERSECT",EDGE,{"derivedFrom":[makeQuery(id+"F5.boolean.opBoolean","SPLIT",FACE,{"disambiguationData":[TD([makeQuery(id+"F2.opExtrude","SWEPT_FACE",FACE,{"disambiguationData":[OSD([subQ5])]})])],"derivedFrom":makeQuery(id+"F3.boolean.opBoolean","COPY",FACE,{"derivedFrom":makeQuery(id+"F3.opExtrude","CAP_FACE",FACE,{"disambiguationData":[OSD([subQ5,subQ1,subQ6,subQ7,subQ4,subQ3,subQ2,subQ0])],"isStart":false})})}),makeQuery(id+"F8.opExtrude","SWEPT_FACE",FACE,{"disambiguationData":[OSD([sQuery(id+"F7.wireOp",EDGE,"E67")])]})]});}
            var Q5;
            Q5=makeQuery(id+"F8.boolean.opBoolean","INTERSECT",EDGE,{"disambiguationData":[OD(0.0)],"derivedFrom":[makeQuery(id+"F5.opExtrude","SWEPT_FACE",FACE,{"disambiguationData":[OSD([sQuery(id+"F4.wireOp",EDGE,"E30")])]}),makeQuery(id+"F8.opExtrude","SWEPT_FACE",FACE,{"disambiguationData":[OSD([sQuery(id+"F7.wireOp",EDGE,"E67")])]})]});
            fillet(context, id + "F14", {"entities" : qUnion([Q0, Q1, Q2, Q3, Q4, Q5]), "radius" : 3 * mm, "tangentPropagation" : true, "allowEdgeOverflow" : false});
        }
        {
            var Q0;
            Q0=makeQuery(id+"F1.opExtrude","CAP_EDGE",EDGE,{"disambiguationData":[OSD([sQuery(id+"F0.wireOp",EDGE,"E1.bottom")])],"isStart":false});
            fillet(context, id + "F15", {"entities" : qUnion([Q0]), "radius" : 2 * mm, "tangentPropagation" : true, "allowEdgeOverflow" : false});
        }
        {
            var Q0;
            {var subQ0=sQuery(id+"F0.wireOp",EDGE,"E21.filletArc");var subQ1=sQuery(id+"F0.wireOp",EDGE,"E7");var subQ2=sQuery(id+"F0.wireOp",EDGE,"E6");var subQ3=sQuery(id+"F0.wireOp",EDGE,"E5");var subQ4=sQuery(id+"F0.wireOp",EDGE,"E4");var subQ5=sQuery(id+"F0.wireOp",EDGE,"E22.filletArc");var subQ6=sQuery(id+"F0.wireOp",EDGE,"E1.bottom");var subQ7=sQuery(id+"F0.wireOp",EDGE,"E1.right");var subQ8=sQuery(id+"F0.wireOp",EDGE,"E1.top");var subQ9=sQuery(id+"F0.wireOp",EDGE,"E1.left");var subQ10=sQuery(id+"F0.wireOp",EDGE,"E23.filletArc");var subQ11=sQuery(id+"F0.wireOp",EDGE,"E24.filletArc");Q0=makeQuery(id+"F2.boolean.opBoolean","SPLIT",FACE,{"disambiguationData":[TD([makeQuery(id+"F1.opExtrude","SWEPT_FACE",FACE,{"disambiguationData":[OSD([subQ6])]})])],"derivedFrom":makeQuery(id+"F1.opExtrude","CAP_FACE",FACE,{"disambiguationData":[OSD([subQ6,subQ8,subQ9,subQ7,subQ4,subQ3,subQ2,subQ1,subQ0,subQ5,subQ10,subQ11])],"isStart":true})});}
            var sketch = newSketch(context, id + "F16", { "sketchPlane" : qUnion([Q0])});
            skLineSegment(sketch, "E79", {"start": v(0, 74.25) * mm, "end": v(0, 104.25) * mm, "construction": true});
            skPoint(sketch, "E79.endSnap0", {"position": v(0, 74.25) * mm});
            skCircle(sketch, "E80", {"center": v(0, 104.25) * mm, "radius": 6 * mm});
            skArc(sketch, "E81", {"start": v(15, 104.25) * mm, "mid": v(0, 119.25) * mm, "end": v(-15, 104.25) * mm});
            skLineSegment(sketch, "E82", {"start": v(-15, 104.25) * mm, "end": v(-15, 92.25) * mm});
            skLineSegment(sketch, "E83", {"start": v(-15, 92.25) * mm, "end": v(-33, 74.25) * mm});
            skLineSegment(sketch, "E84", {"start": v(15, 104.25) * mm, "end": v(15, 92.25) * mm});
            skLineSegment(sketch, "E85", {"start": v(15, 92.25) * mm, "end": v(33, 74.25) * mm});
            skLineSegment(sketch, "E86", {"start": v(-74.25, 0) * mm, "end": v(74.25, 0) * mm, "construction": true});
            skArc(sketch, "E87.MirrorCS", {"start": v(-15, 104.25) * mm, "mid": v(0, 119.25) * mm, "end": v(15, 104.25) * mm});
            skArc(sketch, "E88.MirrorCS", {"start": v(-15, -104.25) * mm, "mid": v(0, -119.25) * mm, "end": v(15, -104.25) * mm});
            skLineSegment(sketch, "E89.MirrorCS", {"start": v(15, -104.25) * mm, "end": v(15, -92.25) * mm});
            skLineSegment(sketch, "E90.MirrorCS", {"start": v(15, -92.25) * mm, "end": v(33, -74.25) * mm});
            skLineSegment(sketch, "E91.MirrorCS", {"start": v(-15, -92.25) * mm, "end": v(-33, -74.25) * mm});
            skLineSegment(sketch, "E92.MirrorCS", {"start": v(-15, -104.25) * mm, "end": v(-15, -92.25) * mm});
            skArc(sketch, "E93.MirrorCS", {"start": v(15, -104.25) * mm, "mid": v(0, -119.25) * mm, "end": v(-15, -104.25) * mm});
            skCircle(sketch, "E94.MirrorC", {"center": v(0, -104.25) * mm, "radius": 6 * mm});
            skSolve(sketch);
        }
        {
            var Q0;
            Q0=makeQuery(id+"F16.imprint","IMPRINT",FACE,{"disambiguationData":[TD([[makeQuery(id+"F16.imprint","IMPRINT",EDGE,{"derivedFrom":sQuery(id+"F16.wireOp",EDGE,"E80")}),-1.0]])]});
            var Q1;
            {var subQ1=sQuery(id+"F16.wireOp",EDGE,"E90.MirrorCS");Q1=makeQuery(id+"F16.imprint","IMPRINT",FACE,{"disambiguationData":[TD([[makeQuery(id+"F16.imprint","IMPRINT",EDGE,{"derivedFrom":subQ1}),1.0]])]});}
            var Q2;
            Q2=makeQuery(id+"F2.opExtrude","CAP_FACE",FACE,{"disambiguationData":[OSD([sQuery(id+"F0.wireOp",EDGE,"E12"),sQuery(id+"F0.wireOp",EDGE,"E13"),sQuery(id+"F0.wireOp",EDGE,"E14"),sQuery(id+"F0.wireOp",EDGE,"E15"),sQuery(id+"F0.wireOp",EDGE,"E17.filletArc"),sQuery(id+"F0.wireOp",EDGE,"E18.filletArc"),sQuery(id+"F0.wireOp",EDGE,"E19.filletArc"),sQuery(id+"F0.wireOp",EDGE,"E20.filletArc"),sQuery(id+"F0.wireOp",EDGE,"E25.0"),sQuery(id+"F0.wireOp",EDGE,"E25.1"),sQuery(id+"F0.wireOp",EDGE,"E25.2"),sQuery(id+"F0.wireOp",EDGE,"E25.3"),sQuery(id+"F0.wireOp",EDGE,"E25.4"),sQuery(id+"F0.wireOp",EDGE,"E25.5"),sQuery(id+"F0.wireOp",EDGE,"E25.6"),sQuery(id+"F0.wireOp",EDGE,"E25.7")])],"isStart":false});
            extrude(context, id + "F17", {"entities" : qUnion([Q0, Q1]), "endBound" : BoundingType.UP_TO_SURFACE, "depth" : 25.4 * mm, "endBoundEntityFace" : qUnion([Q2]), "offsetDistance" : 25.4 * mm});
        }
        {
            var Q0;
            {var subQ0=sQuery(id+"F0.wireOp",EDGE,"E21.filletArc");var subQ1=sQuery(id+"F0.wireOp",EDGE,"E7");var subQ2=sQuery(id+"F0.wireOp",EDGE,"E6");var subQ3=sQuery(id+"F0.wireOp",EDGE,"E5");var subQ4=sQuery(id+"F0.wireOp",EDGE,"E4");var subQ5=sQuery(id+"F0.wireOp",EDGE,"E22.filletArc");var subQ6=sQuery(id+"F0.wireOp",EDGE,"E1.bottom");var subQ7=sQuery(id+"F0.wireOp",EDGE,"E1.right");var subQ8=sQuery(id+"F0.wireOp",EDGE,"E1.top");var subQ9=sQuery(id+"F0.wireOp",EDGE,"E1.left");var subQ10=sQuery(id+"F0.wireOp",EDGE,"E23.filletArc");var subQ11=sQuery(id+"F0.wireOp",EDGE,"E24.filletArc");Q0=makeQuery(id+"F2.boolean.opBoolean","SPLIT",FACE,{"disambiguationData":[TD([makeQuery(id+"F1.opExtrude","SWEPT_FACE",FACE,{"disambiguationData":[OSD([subQ6])]})])],"derivedFrom":makeQuery(id+"F1.opExtrude","CAP_FACE",FACE,{"disambiguationData":[OSD([subQ6,subQ8,subQ9,subQ7,subQ4,subQ3,subQ2,subQ1,subQ0,subQ5,subQ10,subQ11])],"isStart":true})});}
            var Q1;
            Q1=makeQuery(id+"F17.opExtrude","CAP_FACE",FACE,{"disambiguationData":[OSD([sQuery(id+"F0.wireOp",EDGE,"E1.top"),sQuery(id+"F16.wireOp",EDGE,"E80"),sQuery(id+"F16.wireOp",EDGE,"E84"),sQuery(id+"F16.wireOp",EDGE,"E85"),sQuery(id+"F16.wireOp",EDGE,"E81"),sQuery(id+"F16.wireOp",EDGE,"E83"),sQuery(id+"F16.wireOp",EDGE,"E82")])],"isStart":false});
            extrude(context, id + "F18", {"entities" : qUnion([Q0]), "endBound" : BoundingType.UP_TO_SURFACE, "depth" : 25.4 * mm, "endBoundEntityFace" : qUnion([Q1]), "offsetDistance" : 25.4 * mm});
        }
    });
